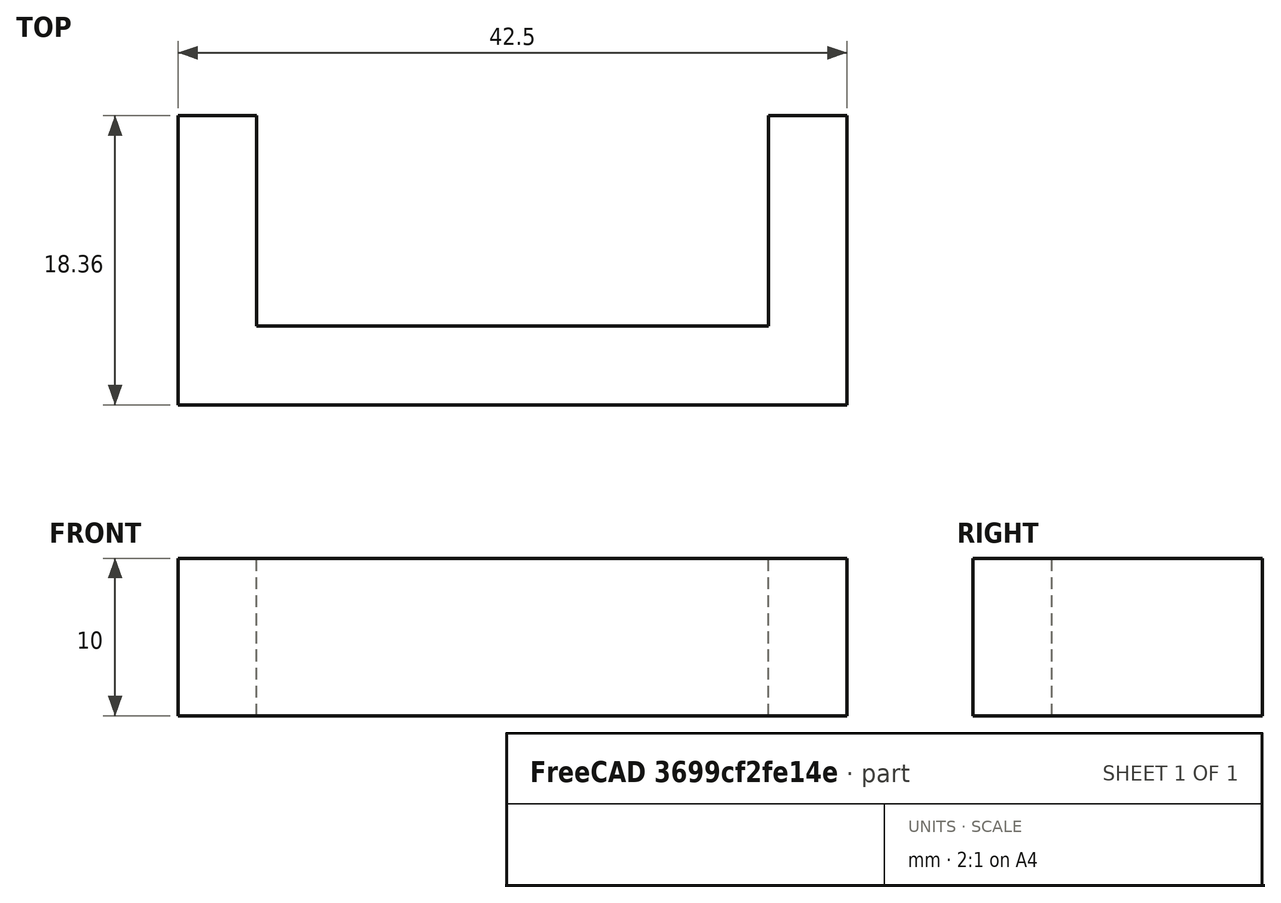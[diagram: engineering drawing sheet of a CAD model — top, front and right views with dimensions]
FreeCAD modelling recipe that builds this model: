
FCSTD DOCUMENT  (FreeCAD 0.17R13217 (Git))
Label: 04-seccion-u
License: All rights reserved
LicenseURL: http://en.wikipedia.org/wiki/All_rights_reserved
objects: Sketcher::SketchObject×1, PartDesign::Pad×1, PartDesign::Body×1
note: 4 computed .brp shape members not serialized (recipe doc carries the construction recipe); baked Part::Feature solids carry a one-line shape summary decoded from their .brp

FEATURE [Sketcher::SketchObject] Sketch
  MapMode = 5
  Support = -> [XY_Plane]
  sketch-geometry (8):
    g0: LineSegment StartX=-21.2484 StartY=0 StartZ=0 EndX=-21.2484 EndY=18.3633 EndZ=0
    g1: LineSegment StartX=-21.2484 StartY=18.3633 StartZ=0 EndX=-16.2484 EndY=18.3633 EndZ=0
    g2: LineSegment StartX=-16.2484 StartY=18.3633 StartZ=0 EndX=-16.2484 EndY=5 EndZ=0
    g3: LineSegment StartX=-16.2484 StartY=5 StartZ=0 EndX=16.2484 EndY=5 EndZ=0
    g4: LineSegment StartX=16.2484 StartY=5 StartZ=0 EndX=16.2484 EndY=18.3633 EndZ=0
    g5: LineSegment StartX=16.2484 StartY=18.3633 StartZ=0 EndX=21.2484 EndY=18.3633 EndZ=0
    g6: LineSegment StartX=21.2484 StartY=18.3633 StartZ=0 EndX=21.2484 EndY=0 EndZ=0
    g7: LineSegment StartX=21.2484 StartY=0 StartZ=0 EndX=-21.2484 EndY=0 EndZ=0
  constraints (21):
    c: PointOnObject(g0,g-1)
    c: Vertical(g0)
    c: Coincident(g0,g1)
    c: Horizontal(g1)
    c: Coincident(g1,g2)
    c: Vertical(g2)
    c: Coincident(g2,g3)
    c: Horizontal(g3)
    c: Coincident(g3,g4)
    c: Vertical(g4)
    c: Coincident(g4,g5)
    c: Horizontal(g5)
    c: Coincident(g5,g6)
    c: PointOnObject(g6,g-1)
    c: Vertical(g6)
    c: Coincident(g6,g7)
    c: Coincident(g7,g0)
    c: Symmetric(g1,g4,g-2)
    c: Symmetric(g0,g6,g-2)
    c: DistanceX(g1,g1) = 5
    c: DistanceY(g0,g2) = 5
FEATURE [PartDesign::Pad] Pad
  Length = 10
  Length2 = 100
  Profile = -> Sketch
  Refine = true
  Type = 0
FEATURE [PartDesign::Body] Body
  Group = -> [Sketch,Pad]
  Origin = -> Origin
  Tip = -> Pad
